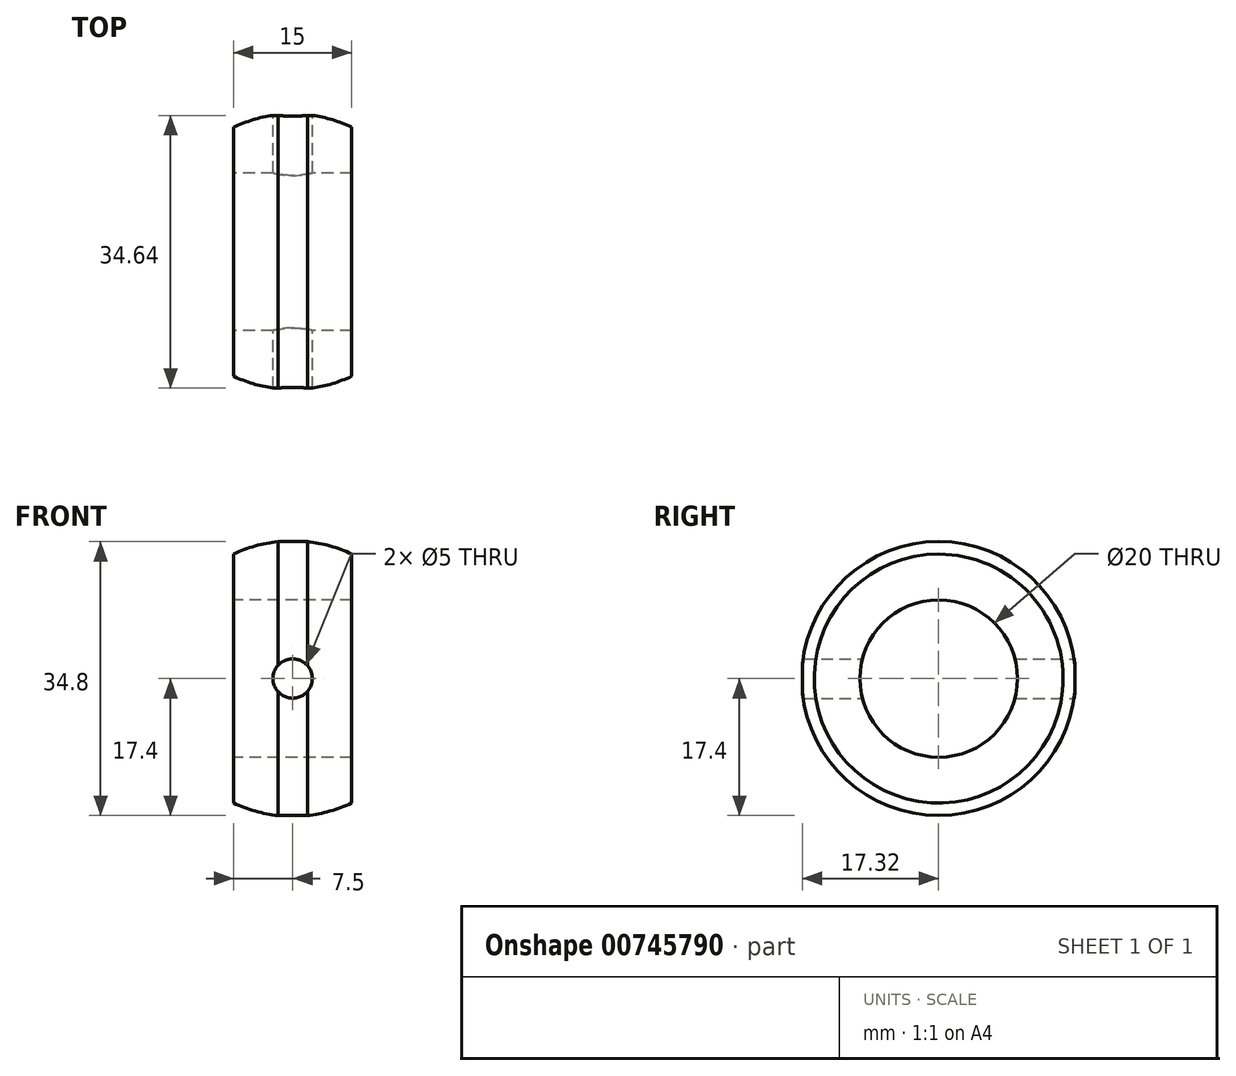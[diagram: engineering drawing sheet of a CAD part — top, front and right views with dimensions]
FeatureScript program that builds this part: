
annotation { "Feature Type Name" : "Feature", "Feature Type Description" : "" }
export const myFeature = defineFeature(function(context is Context, id is Id, definition is map)
    precondition{}
    {
        {
            var Q0;
            Q0=qCreatedBy(makeId("Top.planeOp"),FACE);
            var sketch = newSketch(context, id + "F0", { "sketchPlane" : qUnion([Q0])});
            skArc(sketch, "E0", {"start": v(7.5, 15.81) * mm, "mid": v(4.75, 16.84) * mm, "end": v(1.87, 17.4) * mm});
            skLineSegment(sketch, "E1", {"start": v(-7.5, 10) * mm, "end": v(7.5, 10) * mm});
            skLineSegment(sketch, "E2", {"start": v(-7.5, 15.81) * mm, "end": v(-7.5, 10) * mm});
            skLineSegment(sketch, "E3.0", {"start": v(7.5, 15.81) * mm, "end": v(7.5, 10) * mm});
            skPoint(sketch, "E4.orphan", {"position": v(-7.5, 20.4) * mm});
            skLineSegment(sketch, "E5", {"start": v(-1.87, 17.4) * mm, "end": v(1.87, 17.4) * mm});
            skPoint(sketch, "E5.startSnap0", {"position": v(0, 17.4) * mm});
            skArc(sketch, "E6.trimOffspring", {"start": v(-1.87, 17.4) * mm, "mid": v(-4.75, 16.84) * mm, "end": v(-7.5, 15.81) * mm});
            skPoint(sketch, "E7.orphan", {"position": v(-10.26, 17.4) * mm});
            skLineSegment(sketch, "E8", {"start": v(0, 0) * mm, "end": v(8.4, 0) * mm, "construction": true});
            skSolve(sketch);
        }
        {
            var Q0;
            Q0=makeQuery(id+"F0.imprint","IMPRINT",FACE,{"disambiguationData":[TD([[makeQuery(id+"F0.imprint","IMPRINT",EDGE,{"derivedFrom":sQuery(id+"F0.wireOp",EDGE,"E0")}),1.0]])]});
            var Q1;
            Q1=sQuery(id+"F0.wireOp",EDGE,"E8");
            revolve(context, id + "F1", {"surfaceOperationType" : NewSurfaceOperationType.NEW, "entities" : qUnion([Q0]), "axis" : qUnion([Q1]), "revolveType" : RevolveType.FULL});
        }
        {
            var Q0;
            Q0=qCreatedBy(makeId("Front.planeOp"),FACE);
            var sketch = newSketch(context, id + "F2", { "sketchPlane" : qUnion([Q0])});
            skCircle(sketch, "E9", {"center": v(0, 0) * mm, "radius": 2.5 * mm});
            skSolve(sketch);
        }
        {
            var Q0;
            Q0 = qSketchRegion(id + "F2", true);
            extrude(context, id + "F3", {"entities" : qUnion([Q0]), "operationType" : NewBodyOperationType.REMOVE, "depth" : 25 * mm, "offsetDistance" : 25 * mm, "hasSecondDirection" : true, "secondDirectionOppositeDirection" : true, "secondDirectionDepth" : 25 * mm});
        }
    });
